# Revit family: Actuation Pilot Container-JCI_Sapphire_Plus-(3L)Novec1230
name_source: partatom
category: Specialty Equipment
revit_build: Autodesk Revit 2017 (Build: 20171027_0315(x64)
units: mm (PartAtom-declared; Revit-internal decimal feet)

## family parameters
Always vertical = No
Cut with Voids When Loaded = No
OmniClass Number = 23.29.33.13.11
Part Type = Normal
Room Calculation Point = No
Round Connector Dimension = Use Diameter
Shared = No
Work Plane-Based = Yes

## types (7) — shared parameters
Container Material = JCI - Metal - Steel - Paint - Red
Date Modified = YYYY/MM/DD
Default Elevation = 0.00 mm
Equipment Abbreviation = APC
Family Version = 1.0
Fire Suppression Agent = 3M™ Novec™ 1230 Fire Protection Fluid
Flexible Hose Dia = 6.35 mm
Flexible Hose Length = 710.00 mm
Manufacturer = Johnson Controls, Inc.
Material = JCI - Metal - Stainless Steel - Satin
Model Disclaimer = For More Information Contact JOHNSON CONTROLS
Operating Temperature = 122 °F
Product Documentation Link = http://www.sapphireplus.com
Product Material = JCI - Metal - Stainless Steel - Satin ; JCI - Plastic - Red - Matte
Product Page URL = http://www.sapphireplus.com
URL = https://www.ansul.com
Unit Assembly = Sapphire Plus_Actuation Pilot Container

## per-type parameters (varying)
| type | Container Size | Container Tank Size | Description | Model | Tank Radius |
| TPED 50 degC | 3L | 3 | 3L  Actuation Pilot Container | 304700009 | 50.00 mm |
| TPED 65 degC | 3L | 3 | 3L  Actuation Pilot Container | 304700012 | 50.00 mm |
| DOT 50 degC | 3.4L | 3.4 | 3.4L  Actuation Pilot Container | 304700010 | 66.00 mm |
| DOT 65 degC | 3.4L | 3.4 | 3.4L  Actuation Pilot Container | 304700013 | 66.00 mm |
| TPED | 3L | 3 | 3L  Actuation Pilot Container | 304700008 | 50.00 mm |
| PESO 50 degC | 3L | 3 | 3L  Actuation Pilot Container | 304700007 | 50.00 mm |
| PESO 65 degC | 3L | 3 | 3L  Actuation Pilot Container | 304700011 | 50.00 mm |

## geometry (parser evidence)
native form markers: Sweep x29
no freeform markers — native parametric forms only
